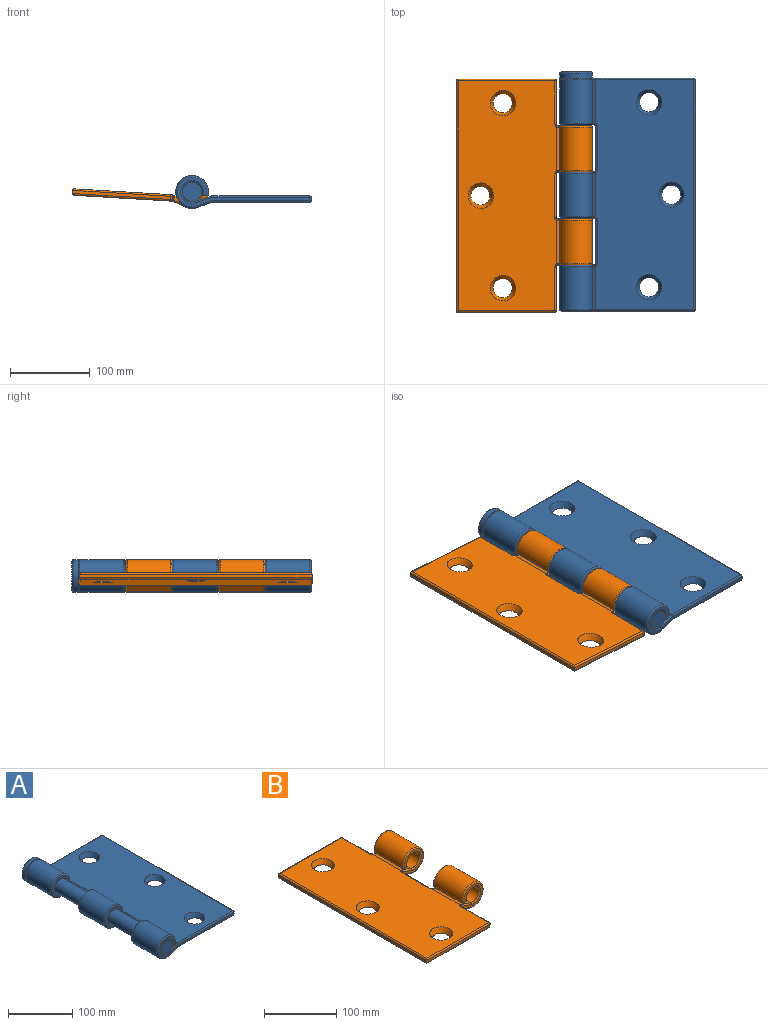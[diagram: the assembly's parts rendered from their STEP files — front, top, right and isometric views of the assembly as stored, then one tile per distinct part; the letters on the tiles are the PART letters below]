
ASSEMBLY  parts=2 mates=1
PART A: 113 faces, bbox 172x300.3x44.6 mm
  f0: cylinder r=12.5mm len=54.4mm, axis (0,1,0), area 3703.3mm2, adj f2,f8,f89,f102
  f1: cylinder r=12.5mm len=54.4mm, axis (0,1,0), area 3565.2mm2, adj f3,f70,f76,f80
  f2: plane 55.15x20.23mm, normal (-0.32,0,0.95), area 1161mm2, adj f0,f91,f92,f103,f105
  f3: plane 55.89x20.23mm, normal (-0.32,0,0.95), area 1161.6mm2, adj f1,f65,f67,f82,f84,f100
  f4: plane 54.63x17.59mm, normal (0.34,0,-0.94), area 1016.4mm2, adj f6,f14,f81,f83,f97
  f5: plane 54.63x17.59mm, normal (0.34,0,-0.94), area 1016.4mm2, adj f7,f14,f64,f68,f71
  f6: cylinder r=20.5mm len=54.4mm, axis (0,1,0), area 5913.6mm2, adj f4,f8,f85,f98
  f7: cylinder r=20.5mm len=54.4mm, axis (0,1,0), area 5913.6mm2, adj f5,f9,f66,f72
  f8: plane 56.67x8.7mm, normal (0,0,-1), area 473.3mm2, adj f0,f6,f18,f87,f98,f102
  f9: plane 54.4x5.69mm, normal (0,0,-1), area 309.8mm2, adj f7,f69,f75,f76
  f10: cylinder r=12.5mm len=54.4mm, axis (0,1,0), area 3565.2mm2, adj f11,f54,f58,f95
  f11: plane 55.15x20.23mm, normal (-0.32,0,0.95), area 1161mm2, adj f10,f60,f63,f93,f94
  f12: plane 288x122.68mm, normal (0,0,1), area 32720.1mm2, adj f20,f21,f22,f33,f35,f36,f57,f59
  f13: plane 288x4mm, normal (1,0,0), area 1152mm2, adj f36,f37,f41,f42
  f14: plane 288.07x123.23mm, normal (0,0,-1), area 33829.6mm2, adj f4,f5,f15,f20,f21,f22,f38,f42
  f15: plane 54.63x17.59mm, normal (0.34,0,-0.94), area 1016.4mm2, adj f14,f16,f48,f49,f51
  f16: cylinder r=20.5mm len=54.4mm, axis (0,1,0), area 5913.6mm2, adj f15,f17,f50,f53
  f17: plane 54.4x5.69mm, normal (0,0,-1), area 309.8mm2, adj f16,f52,f54,f55
  f18: plane 166x37mm, normal (0,-1,0), area 921.7mm2, adj f8,f35,f41,f44,f97,f98,f102,f103
  f19: plane 132.95x7.44mm, normal (0,1,0), area 522mm2, adj f33,f37,f38,f51,f60,f110
  f20: cone r=12mm half-angle=26.6deg, axis (0,0,1), area 786.8mm2, adj f12,f14
  f21: cone r=12mm half-angle=26.6deg, axis (0,0,1), area 786.8mm2, adj f12,f14
  f22: cone r=12mm half-angle=26.6deg, axis (0,0,1), area 786.8mm2, adj f12,f14
  f23: plane 54.4x4mm, normal (-1,0,0), area 217.6mm2, adj f29,f30,f46,f59
  f24: plane 41.44x37mm, normal (0,1,0), area 414mm2, adj f29,f45,f64,f66,f67,f69,f70
  f25: plane 41x37mm, normal (0,-1,0), area 413.9mm2, adj f30,f49,f50,f52,f94,f95
  f26: plane 54.4x4mm, normal (-1,0,0), area 217.6mm2, adj f31,f32,f77,f88
  f27: plane 41x37mm, normal (0,1,0), area 413.9mm2, adj f31,f83,f85,f87,f89,f91
  f28: plane 41x37mm, normal (0,-1,0), area 413.9mm2, adj f32,f68,f72,f75,f80,f82
  f29: cylinder r=2mm len=4mm, axis (0,0,1), area 12.1mm2, adj f23,f24,f45,f57,f65
  f30: cylinder r=2mm len=4.59mm, axis (0,0,-1), area 12.3mm2, adj f23,f25,f47,f48,f61,f93
  f31: cylinder r=2mm len=4.59mm, axis (0,0,1), area 12.3mm2, adj f26,f27,f79,f81,f90,f92
  f32: cylinder r=2mm len=4.59mm, axis (0,0,-1), area 12.3mm2, adj f26,f28,f71,f74,f84,f86
  f33: cylinder r=2mm len=122.68mm, axis (1,0,0), area 385.4mm2, adj f12,f19,f34,f62
  f34: sphere r=2mm, area 6.3mm2, adj f33,f36,f37
  f35: cylinder r=2mm len=122.68mm, axis (-1,0,0), area 385.4mm2, adj f12,f18,f39,f104
  f36: cylinder r=2mm len=288mm, axis (0,1,0), area 904.8mm2, adj f12,f13,f34,f39
  f37: cylinder r=2mm len=4mm, axis (0,0,-1), area 12.6mm2, adj f13,f19,f34,f40
  f38: cylinder r=2mm len=123.35mm, axis (-1,0,0), area 387mm2, adj f14,f19,f40,f51
  f39: sphere r=2mm, area 6.3mm2, adj f35,f36,f41
  f40: sphere r=2mm, area 4mm2, adj f37,f38,f42
  f41: cylinder r=2mm len=4mm, axis (0,0,1), area 12.6mm2, adj f13,f18,f39,f43
  f42: cylinder r=2mm len=288mm, axis (0,1,0), area 904.8mm2, adj f13,f14,f40,f43
  f43: sphere r=2mm, area 6.3mm2, adj f41,f42,f44
  f44: cylinder r=2mm len=123.35mm, axis (1,0,0), area 387mm2, adj f14,f18,f43,f97
  f45: torus R=4mm, axis (0,0,1), area 10.6mm2, adj f14,f24,f29,f46,f64
  f46: cylinder r=2mm len=54.4mm, axis (0,1,0), area 170.9mm2, adj f14,f23,f45,f47
  f47: torus R=4mm, axis (0,0,1), area 9.2mm2, adj f14,f30,f46,f48
  f48: bspline ~2.47x2.33mm, area 3.5mm2, adj f14,f15,f30,f47,f49
  f49: cylinder r=2mm len=16.94mm, axis (-0.94,0,-0.34), area 54.3mm2, adj f15,f25,f48,f50
  f50: torus R=18.5mm, axis (0,1,0), area 326.9mm2, adj f16,f25,f49,f52
  f51: cylinder r=2mm len=18.59mm, axis (-0.94,0,-0.34), area 59.2mm2, adj f15,f19,f38,f53,f107
  f52: cylinder r=2mm len=5.69mm, axis (-1,0,0), area 15.3mm2, adj f17,f25,f50,f96
  f53: torus R=18.5mm, axis (0,-1,0), area 326.9mm2, adj f16,f51,f55,f107
  f54: cylinder r=2mm len=54.4mm, axis (0,1,0), area 193.6mm2, adj f10,f17,f56,f96
  f55: cylinder r=2mm len=5.69mm, axis (-1,0,0), area 15.3mm2, adj f17,f53,f56,f107
  f56: sphere r=2mm, area 6.9mm2, adj f54,f55,f58
  f57: torus R=4mm, axis (0,0,-1), area 8.1mm2, adj f12,f29,f59,f99
  f58: torus R=14.5mm, axis (0,-1,0), area 217.9mm2, adj f10,f56,f60,f107
  f59: cylinder r=2mm len=54.4mm, axis (0,-1,0), area 170.9mm2, adj f12,f23,f57,f61
  f60: cylinder r=2mm len=20.87mm, axis (0.95,0,0.32), area 67mm2, adj f11,f19,f58,f62,f107
  f61: torus R=4mm, axis (0,0,-1), area 8.6mm2, adj f12,f30,f59,f63,f93
  f62: sphere r=2mm, area 1.3mm2, adj f33,f60,f63
  f63: cylinder r=2mm len=55.41mm, axis (0,-1,0), area 35.6mm2, adj f11,f12,f61,f62,f93
  f64: cylinder r=2mm len=18.26mm, axis (0.94,0,0.34), area 57.2mm2, adj f5,f14,f24,f45,f66
  f65: bspline ~3.27x2.99mm, area 5.5mm2, adj f3,f29,f67,f99
  f66: torus R=18.5mm, axis (0,1,0), area 326.9mm2, adj f7,f24,f64,f69
  f67: cylinder r=2mm len=18.54mm, axis (-0.95,0,-0.32), area 59.3mm2, adj f3,f24,f65,f70
  f68: cylinder r=2mm len=16.94mm, axis (-0.94,0,-0.34), area 54.3mm2, adj f5,f28,f71,f72
  f69: cylinder r=2mm len=5.69mm, axis (1,0,0), area 15.3mm2, adj f9,f24,f66,f73
  f70: torus R=14.5mm, axis (0,1,0), area 217.9mm2, adj f1,f24,f67,f73
  f71: bspline ~2.47x2.33mm, area 3.5mm2, adj f5,f14,f32,f68,f74
  f72: torus R=18.5mm, axis (0,1,0), area 326.9mm2, adj f7,f28,f68,f75
  f73: sphere r=2mm, area 9.2mm2, adj f69,f70,f76
  f74: torus R=4mm, axis (0,0,1), area 9.2mm2, adj f14,f32,f71,f77
  f75: cylinder r=2mm len=5.69mm, axis (-1,0,0), area 15.3mm2, adj f9,f28,f72,f78
  f76: cylinder r=2mm len=54.4mm, axis (0,1,0), area 193.6mm2, adj f1,f9,f73,f78
  f77: cylinder r=2mm len=54.4mm, axis (0,1,0), area 170.9mm2, adj f14,f26,f74,f79
  f78: sphere r=2mm, area 6.9mm2, adj f75,f76,f80
  f79: torus R=4mm, axis (0,0,1), area 9.2mm2, adj f14,f31,f77,f81
  f80: torus R=14.5mm, axis (0,1,0), area 217.9mm2, adj f1,f28,f78,f82
  f81: bspline ~2.47x2.33mm, area 3.5mm2, adj f4,f14,f31,f79,f83
  f82: cylinder r=2mm len=18.54mm, axis (0.95,0,0.32), area 59.3mm2, adj f3,f28,f80,f84
  f83: cylinder r=2mm len=16.94mm, axis (0.94,0,0.34), area 54.3mm2, adj f4,f27,f81,f85
  f84: bspline ~3.27x2.99mm, area 5.5mm2, adj f3,f32,f82,f101
  f85: torus R=18.5mm, axis (0,1,0), area 326.9mm2, adj f6,f27,f83,f87
  f86: torus R=4mm, axis (0,0,-1), area 8.1mm2, adj f12,f32,f88,f101
  f87: cylinder r=2mm len=8.42mm, axis (1,0,0), area 19.6mm2, adj f8,f27,f85,f89
  f88: cylinder r=2mm len=54.4mm, axis (0,-1,0), area 170.9mm2, adj f12,f26,f86,f90
  f89: torus R=14.5mm, axis (0,1,0), area 222mm2, adj f0,f27,f87,f91
  f90: torus R=4mm, axis (0,0,-1), area 8.1mm2, adj f12,f31,f88,f106
  f91: cylinder r=2mm len=18.54mm, axis (-0.95,0,-0.32), area 59.3mm2, adj f2,f27,f89,f92
  f92: bspline ~3.27x2.99mm, area 5.5mm2, adj f2,f31,f91,f106
  f93: bspline ~3.65x3.11mm, area 5.9mm2, adj f11,f30,f61,f63,f94
  f94: cylinder r=2mm len=18.54mm, axis (0.95,0,0.32), area 59.3mm2, adj f11,f25,f93,f95
  f95: torus R=14.5mm, axis (0,1,0), area 217.9mm2, adj f10,f25,f94,f96
  f96: sphere r=2mm, area 6.9mm2, adj f52,f54,f95
  f97: cylinder r=2mm len=18.59mm, axis (0.94,0,0.34), area 59.2mm2, adj f4,f18,f44,f98
  f98: torus R=18.5mm, axis (0,-1,0), area 330.2mm2, adj f6,f8,f18,f97
  f99: sphere r=2mm, area 1mm2, adj f57,f65,f100
  f100: cylinder r=2mm len=55.89mm, axis (0,-1,0), area 36mm2, adj f3,f12,f99,f101
  f101: sphere r=2mm, area 1mm2, adj f84,f86,f100
  f102: torus R=14.5mm, axis (0,-1,0), area 225mm2, adj f0,f8,f18,f103
  f103: cylinder r=2mm len=20.87mm, axis (-0.95,0,-0.32), area 67mm2, adj f2,f18,f102,f104
  f104: sphere r=2mm, area 1.3mm2, adj f35,f103,f105
  f105: cylinder r=2mm len=55.15mm, axis (0,-1,0), area 35.5mm2, adj f2,f12,f104,f106
  f106: sphere r=2mm, area 1mm2, adj f90,f92,f105
  f107: plane 41x41mm, normal (0,-1,0), area 457.3mm2, adj f51,f53,f55,f58,f60,f108,f110
  f108: cylinder r=12.25mm len=292mm, axis (0,1,0), area 22475mm2, adj f107,f109
  f109: plane 24.5x24.5mm, normal (0,-1,0), area 471.4mm2, adj f108
  f110: cylinder r=20.5mm len=41mm, axis (0,-1,0), area 772.8mm2, adj f19,f107,f112
  f111: plane 37x37mm, normal (0,1,0), area 1075.2mm2, adj f112
  f112: torus R=18.5mm, axis (0,1,0), area 390.3mm2, adj f110,f111
PART B: 86 faces, bbox 171.7x292x44.4 mm
  f0: cylinder r=12.5mm len=54.4mm, axis (0,1,0), area 3703.3mm2, adj f2,f8,f67,f75
  f1: cylinder r=12.5mm len=54.4mm, axis (0,1,0), area 3565.2mm2, adj f3,f31,f32,f35
  f2: plane 56.21x20.54mm, normal (0.32,0,0.95), area 1179.8mm2, adj f0,f12,f51,f57,f62,f63,f68,f72
  f3: plane 56.21x20.54mm, normal (0.32,0,0.95), area 1179.8mm2, adj f1,f12,f34,f38,f39,f42,f43,f48
  f4: plane 54.85x17.59mm, normal (-0.34,0,-0.94), area 1016.5mm2, adj f6,f14,f61,f66,f84,f85
  f5: plane 54.85x17.59mm, normal (-0.34,0,-0.94), area 1016.5mm2, adj f7,f14,f37,f41,f49,f55
  f6: cylinder r=20.5mm len=54.4mm, axis (0,1,0), area 5820.5mm2, adj f4,f70,f77,f82
  f7: cylinder r=20.5mm len=54.4mm, axis (0,1,0), area 5913.6mm2, adj f5,f9,f33,f44
  f8: plane 54.4x6.8mm, normal (0,0,-1), area 369.8mm2, adj f0,f71,f77,f78
  f9: plane 54.4x5.69mm, normal (0,0,-1), area 309.8mm2, adj f7,f30,f32,f40
  f10: plane 123x4mm, normal (0,-1,0), area 492mm2, adj f13,f53,f64,f73
  f11: plane 125x4mm, normal (0,1,0), area 500mm2, adj f13,f23,f52,f79
  f12: plane 288x123mm, normal (0,0,1), area 32665.2mm2, adj f2,f3,f15,f16,f17,f42,f46,f47
  f13: plane 292x4mm, normal (-1,0,0), area 1168mm2, adj f10,f11,f47,f76
  f14: plane 288x123.06mm, normal (0,0,-1), area 33720.8mm2, adj f4,f5,f15,f16,f17,f41,f45,f50
  f15: cone r=12mm half-angle=26.6deg, axis (0,0,1), area 786.8mm2, adj f12,f14
  f16: cone r=12mm half-angle=26.6deg, axis (0,0,1), area 786.8mm2, adj f12,f14
  f17: cone r=12mm half-angle=26.6deg, axis (0,0,1), area 786.8mm2, adj f12,f14
  f18: plane 54.4x4mm, normal (1,0,0), area 217.6mm2, adj f25,f54,f64,f65
  f19: plane 41x37mm, normal (0,-1,0), area 413.9mm2, adj f25,f35,f39,f40,f44,f49
  f20: plane 54.4x4mm, normal (1,0,0), area 217.6mm2, adj f26,f27,f46,f50
  f21: plane 41x37mm, normal (0,-1,0), area 413.9mm2, adj f26,f62,f66,f67,f70,f71
  f22: plane 41x37mm, normal (0,1,0), area 413.9mm2, adj f27,f30,f31,f33,f34,f37
  f23: plane 56.4x4mm, normal (1,0,0), area 225.6mm2, adj f11,f28,f58,f81
  f24: plane 41x37mm, normal (0,1,0), area 413.9mm2, adj f28,f72,f75,f78,f82,f84
  f25: cylinder r=2mm len=4.59mm, axis (0,0,-1), area 12.3mm2, adj f18,f19,f43,f48,f55,f60
  f26: cylinder r=2mm len=4.59mm, axis (0,0,-1), area 12.3mm2, adj f20,f21,f51,f56,f57,f61
  f27: cylinder r=2mm len=4.59mm, axis (0,0,1), area 12.3mm2, adj f20,f22,f38,f41,f42,f45
  f28: cylinder r=2mm len=4.59mm, axis (0,0,1), area 12.3mm2, adj f23,f24,f63,f68,f83,f85
  f29: sphere r=2mm, area 4.7mm2, adj f30,f31,f32
  f30: cylinder r=2mm len=5.69mm, axis (1,0,0), area 15.3mm2, adj f9,f22,f29,f33
  f31: torus R=14.5mm, axis (0,-1,0), area 217.9mm2, adj f1,f22,f29,f34
  f32: cylinder r=2mm len=54.4mm, axis (0,1,0), area 193.6mm2, adj f1,f9,f29,f36
  f33: torus R=18.5mm, axis (0,-1,0), area 326.9mm2, adj f7,f22,f30,f37
  f34: cylinder r=2mm len=18.54mm, axis (-0.95,0,0.32), area 59.3mm2, adj f3,f22,f31,f38
  f35: torus R=14.5mm, axis (0,-1,0), area 217.9mm2, adj f1,f19,f36,f39
  f36: sphere r=2mm, area 7.1mm2, adj f32,f35,f40
  f37: cylinder r=2mm len=16.94mm, axis (0.94,0,-0.34), area 54.3mm2, adj f5,f22,f33,f41
  f38: bspline ~2.75x2.54mm, area 6mm2, adj f3,f27,f34,f42
  f39: cylinder r=2mm len=18.54mm, axis (0.95,0,-0.32), area 59.3mm2, adj f3,f19,f35,f43
  f40: cylinder r=2mm len=5.69mm, axis (-1,0,0), area 15.3mm2, adj f9,f19,f36,f44
  f41: bspline ~2.47x2.33mm, area 3.5mm2, adj f5,f14,f27,f37,f45
  f42: torus R=4mm, axis (0,0,-1), area 8.7mm2, adj f3,f12,f27,f38,f46
  f43: bspline ~3.65x3.11mm, area 6mm2, adj f3,f25,f39,f48
  f44: torus R=18.5mm, axis (0,-1,0), area 326.9mm2, adj f7,f19,f40,f49
  f45: torus R=4mm, axis (0,0,1), area 9.2mm2, adj f14,f27,f41,f50
  f46: cylinder r=2mm len=54.4mm, axis (0,1,0), area 170.9mm2, adj f12,f20,f42,f51
  f47: cylinder r=2mm len=292mm, axis (0,1,0), area 911.1mm2, adj f12,f13,f52,f53
  f48: torus R=4mm, axis (0,0,-1), area 8.7mm2, adj f3,f12,f25,f43,f54
  f49: cylinder r=2mm len=16.94mm, axis (-0.94,0,0.34), area 54.3mm2, adj f5,f19,f44,f55
  f50: cylinder r=2mm len=54.4mm, axis (0,-1,0), area 170.9mm2, adj f14,f20,f45,f56
  f51: torus R=4mm, axis (0,0,-1), area 8.7mm2, adj f2,f12,f26,f46,f57
  f52: cylinder r=2mm len=125mm, axis (-1,0,0), area 386.4mm2, adj f11,f12,f47,f58
  f53: cylinder r=2mm len=123mm, axis (1,0,0), area 383.3mm2, adj f10,f12,f47,f59
  f54: cylinder r=2mm len=54.4mm, axis (0,-1,0), area 170.9mm2, adj f12,f18,f48,f59
  f55: bspline ~2.47x2.33mm, area 3.5mm2, adj f5,f14,f25,f49,f60
  f56: torus R=4mm, axis (0,0,1), area 9.2mm2, adj f14,f26,f50,f61
  f57: bspline ~3.65x3.11mm, area 6mm2, adj f2,f26,f51,f62
  f58: cylinder r=2mm len=56.4mm, axis (0,1,0), area 174mm2, adj f12,f23,f52,f63
  f59: sphere r=2mm, area 6.3mm2, adj f53,f54,f64
  f60: torus R=4mm, axis (0,0,1), area 9.2mm2, adj f14,f25,f55,f65
  f61: bspline ~2.47x2.33mm, area 3.5mm2, adj f4,f14,f26,f56,f66
  f62: cylinder r=2mm len=18.54mm, axis (0.95,0,-0.32), area 59.3mm2, adj f2,f21,f57,f67
  f63: torus R=4mm, axis (0,0,-1), area 8.7mm2, adj f2,f12,f28,f58,f68
  f64: cylinder r=2mm len=4mm, axis (0,0,1), area 12.6mm2, adj f10,f18,f59,f69
  f65: cylinder r=2mm len=54.4mm, axis (0,-1,0), area 170.9mm2, adj f14,f18,f60,f69
  f66: cylinder r=2mm len=16.94mm, axis (-0.94,0,0.34), area 54.3mm2, adj f4,f21,f61,f70
  f67: torus R=14.5mm, axis (0,-1,0), area 222mm2, adj f0,f21,f62,f71
  f68: bspline ~3.65x3.11mm, area 6mm2, adj f2,f28,f63,f72
  f69: sphere r=2mm, area 6.3mm2, adj f64,f65,f73
  f70: torus R=18.5mm, axis (0,-1,0), area 324.2mm2, adj f6,f21,f66,f74
  f71: cylinder r=2mm len=6.8mm, axis (-1,0,0), area 17.1mm2, adj f8,f21,f67,f74
  f72: cylinder r=2mm len=18.54mm, axis (-0.95,0,0.32), area 59.3mm2, adj f2,f24,f68,f75
  f73: cylinder r=2mm len=123mm, axis (-1,0,0), area 383.3mm2, adj f10,f14,f69,f76
  f74: sphere r=2mm, area 5.8mm2, adj f70,f71,f77
  f75: torus R=14.5mm, axis (0,-1,0), area 222mm2, adj f0,f24,f72,f78
  f76: cylinder r=2mm len=292mm, axis (0,1,0), area 911.1mm2, adj f13,f14,f73,f79
  f77: cylinder r=2mm len=54.4mm, axis (0,1,0), area 153.2mm2, adj f6,f8,f74,f80
  f78: cylinder r=2mm len=6.8mm, axis (1,0,0), area 17.1mm2, adj f8,f24,f75,f80
  f79: cylinder r=2mm len=125mm, axis (1,0,0), area 386.4mm2, adj f11,f14,f76,f81
  f80: sphere r=2mm, area 8.1mm2, adj f77,f78,f82
  f81: cylinder r=2mm len=56.4mm, axis (0,-1,0), area 174mm2, adj f14,f23,f79,f83
  f82: torus R=18.5mm, axis (0,-1,0), area 324.2mm2, adj f6,f24,f80,f84
  f83: torus R=4mm, axis (0,0,1), area 9.2mm2, adj f14,f28,f81,f85
  f84: cylinder r=2mm len=16.94mm, axis (0.94,0,-0.34), area 54.3mm2, adj f4,f24,f82,f85
  f85: bspline ~2.47x2.33mm, area 3.5mm2, adj f4,f14,f28,f83,f84
PLACE A t=(-114.94,66.18,-40.5)mm fixed
PLACE B rot(axis=(0,1,0),3.5deg) t=(-115.2,64.98,-39.02)mm
MATE revolute A.f0 <-> B.f0  axis (0,1,0) through (-90.44,-79.82,-35.5)mm
